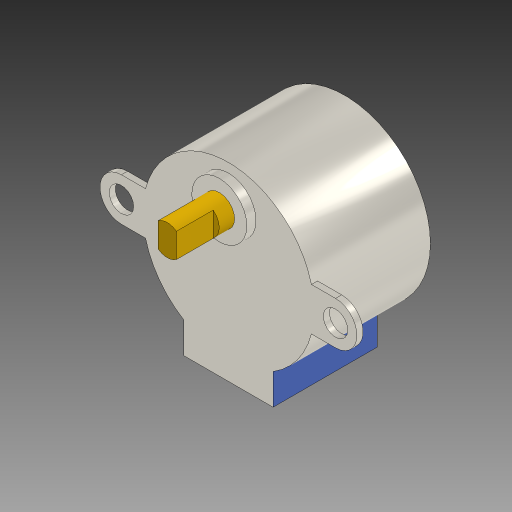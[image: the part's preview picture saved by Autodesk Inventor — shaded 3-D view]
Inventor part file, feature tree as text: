
AUTODESK INVENTOR PART (.ipt)
format: ipt  version: 2023 (Build 270158000, 158)  size: 181,760 bytes
history: native  units: mm
features: extrude x6, sketch x6, other x1
ambient origin geometry x8: Origin, YZ Plane, XZ Plane, XY Plane, X Axis, Y Axis, Z Axis, Center Point
bodies: Body1 (feature_tree)
feature tree (13):
  other  "Těleso1"
  extrude  "Vysunutí1"  Depth=28.0mm
  extrude  "Vysunutí2"  Depth=19.0mm TaperAngle=0.0deg
  extrude  "Vysunutí3"  Depth=4.0mm
  extrude  "Vysunutí4"  Depth=4.0mm
  extrude  "Vysunutí5"  Depth=35.0mm
  extrude  "Vysunutí6"  Depth=17.5mm
  sketch  "Náčrt1"
  sketch  "Náčrt2"
  sketch  "Náčrt3"
  sketch  "Náčrt4"
  sketch  "Náčrt5"
  sketch  "Náčrt6"
